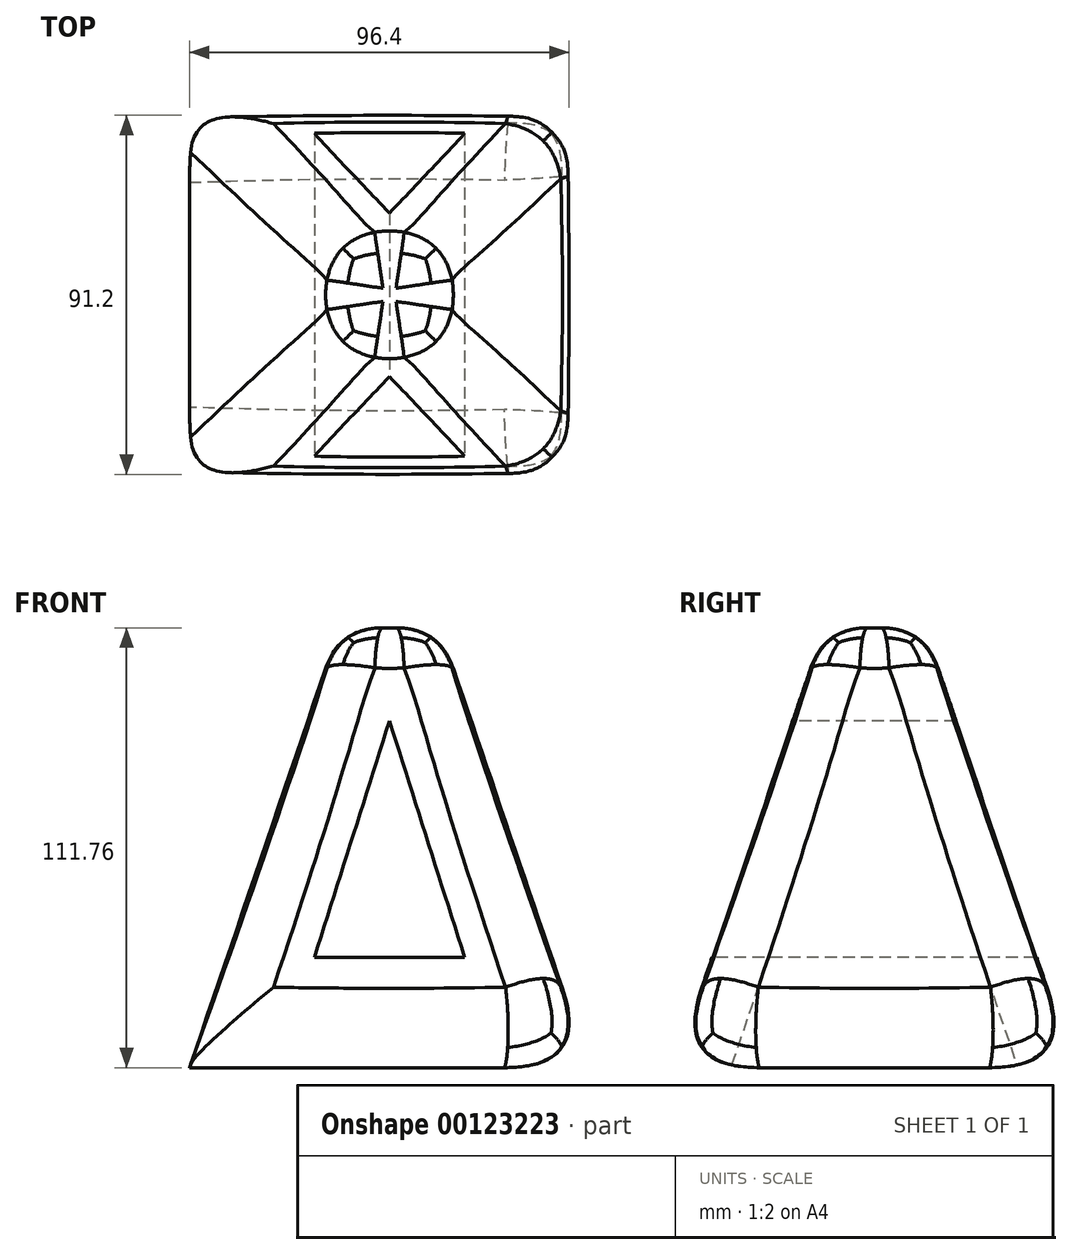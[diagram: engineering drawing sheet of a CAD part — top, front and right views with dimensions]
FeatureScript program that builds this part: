
annotation { "Feature Type Name" : "Feature", "Feature Type Description" : "" }
export const myFeature = defineFeature(function(context is Context, id is Id, definition is map)
    precondition{}
    {
        {
            var Q0;
            Q0=qCreatedBy(makeId("Top.planeOp"),FACE);
            cPlane(context, id + "F0", {"entities" : qUnion([Q0]), "cplaneType" : CPlaneType.OFFSET, "offset" : 111.76 * mm, "width" : 152.4 * mm, "height" : 152.4 * mm});
        }
        {
            var Q0;
            Q0=qCreatedBy(makeId("Top.planeOp"),FACE);
            var sketch = newSketch(context, id + "F1", { "sketchPlane" : qUnion([Q0])});
            skLineSegment(sketch, "E0.bottom", {"start": v(50.8, 50.8) * mm, "end": v(-50.8, 50.8) * mm});
            skLineSegment(sketch, "E0.top", {"start": v(50.8, -50.8) * mm, "end": v(-50.8, -50.8) * mm});
            skLineSegment(sketch, "E0.left", {"start": v(50.8, 50.8) * mm, "end": v(50.8, -50.8) * mm});
            skLineSegment(sketch, "E0.right", {"start": v(-50.8, 50.8) * mm, "end": v(-50.8, -50.8) * mm});
            skPoint(sketch, "E0.middle", {"position": v(0, 0) * mm});
            skSolve(sketch);
        }
        {
            var Q0;
            Q0=qCreatedBy(id+"F0.planeOp",FACE);
            var sketch = newSketch(context, id + "F2", { "sketchPlane" : qUnion([Q0])});
            skCircle(sketch, "E1", {"center": v(0, 0) * mm, "radius": 12.7 * mm});
            skSolve(sketch);
        }
        {
            var Q0;
            Q0=makeQuery(id+"F1.imprint","IMPRINT",FACE,{"disambiguationData":[TD([[makeQuery(id+"F1.imprint","IMPRINT",EDGE,{"derivedFrom":sQuery(id+"F1.wireOp",EDGE,"E0.bottom")}),1.0]])]});
            var Q1;
            Q1=makeQuery(id+"F2.imprint","IMPRINT",FACE,{"disambiguationData":[TD([[makeQuery(id+"F2.imprint","IMPRINT",EDGE,{"derivedFrom":sQuery(id+"F2.wireOp",EDGE,"E1")}),1.0]])]});
            loft(context, id + "F3", {"sheetProfilesArray" : [{ "sheetProfileEntities" : qUnion([Q0]) }, { "sheetProfileEntities" : qUnion([Q1]) }]});
        }
        {
            var Q0;
            {var subQ0=sQuery(id+"F2.wireOp",EDGE,"E1");var subQ1=sQuery(id+"F1.wireOp",EDGE,"E0.top");var subQ2=sQuery(id+"F1.wireOp",EDGE,"E0.right");var subQ3=sQuery(id+"F1.wireOp",EDGE,"E0.left");var subQ4=sQuery(id+"F1.wireOp",EDGE,"E0.bottom");Q0=makeQuery(id+"F3.opLoft","SWEPT_FACE",FACE,{"disambiguationData":[OSD([subQ4,subQ1,subQ3,subQ2,subQ0]),TDD([makeQuery(id+"F1.imprint","INTERSECT",VERTEX,{"derivedFrom":[subQ4,subQ2]}),makeQuery(id+"F1.imprint","INTERSECT",VERTEX,{"derivedFrom":[subQ1,subQ3]}),makeQuery(id+"F1.imprint","INTERSECT",VERTEX,{"derivedFrom":[subQ1,subQ2]}),makeQuery(id+"F1.imprint","IMPRINT",EDGE,{"derivedFrom":subQ1}),makeQuery(id+"F2.imprint","IMPRINT",EDGE,{"derivedFrom":subQ0})])]});}
            var Q1;
            {var subQ0=sQuery(id+"F2.wireOp",EDGE,"E1");var subQ1=sQuery(id+"F1.wireOp",EDGE,"E0.left");var subQ2=sQuery(id+"F1.wireOp",EDGE,"E0.right");var subQ3=sQuery(id+"F1.wireOp",EDGE,"E0.top");var subQ4=sQuery(id+"F1.wireOp",EDGE,"E0.bottom");Q1=makeQuery(id+"F3.opLoft","SWEPT_FACE",FACE,{"disambiguationData":[OSD([subQ4,subQ3,subQ1,subQ2,subQ0]),TDD([makeQuery(id+"F1.imprint","INTERSECT",VERTEX,{"derivedFrom":[subQ4,subQ1]}),makeQuery(id+"F1.imprint","INTERSECT",VERTEX,{"derivedFrom":[subQ3,subQ1]}),makeQuery(id+"F1.imprint","INTERSECT",VERTEX,{"derivedFrom":[subQ3,subQ2]}),makeQuery(id+"F1.imprint","IMPRINT",EDGE,{"derivedFrom":subQ1}),makeQuery(id+"F2.imprint","IMPRINT",EDGE,{"derivedFrom":subQ0})])]});}
            var Q2;
            {var subQ0=sQuery(id+"F2.wireOp",EDGE,"E1");var subQ1=sQuery(id+"F1.wireOp",EDGE,"E0.right");var subQ2=sQuery(id+"F1.wireOp",EDGE,"E0.top");var subQ3=sQuery(id+"F1.wireOp",EDGE,"E0.bottom");var subQ4=sQuery(id+"F1.wireOp",EDGE,"E0.left");Q2=makeQuery(id+"F3.opLoft","SWEPT_FACE",FACE,{"disambiguationData":[OSD([subQ3,subQ2,subQ4,subQ1,subQ0]),TDD([makeQuery(id+"F1.imprint","INTERSECT",VERTEX,{"derivedFrom":[subQ3,subQ4]}),makeQuery(id+"F1.imprint","INTERSECT",VERTEX,{"derivedFrom":[subQ3,subQ1]}),makeQuery(id+"F1.imprint","INTERSECT",VERTEX,{"derivedFrom":[subQ2,subQ1]}),makeQuery(id+"F1.imprint","IMPRINT",EDGE,{"derivedFrom":subQ1}),makeQuery(id+"F2.imprint","IMPRINT",EDGE,{"derivedFrom":subQ0})])]});}
            var Q3;
            Q3=makeQuery(id+"F3.opLoft","SWEPT_FACE",FACE,{"disambiguationData":[OSD([sQuery(id+"F1.wireOp",EDGE,"E0.bottom"),sQuery(id+"F1.wireOp",EDGE,"E0.left"),sQuery(id+"F1.wireOp",EDGE,"E0.right"),sQuery(id+"F2.wireOp",EDGE,"E1")])]});
            fillet(context, id + "F4", {"entities" : qUnion([Q0, Q1, Q2, Q3]), "radius" : 15.24 * mm, "tangentPropagation" : true, "rho" : 0.5, "crossSection" : FilletCrossSection.CONIC, "allowEdgeOverflow" : false});
        }
        {
            var Q0;
            Q0=qCreatedBy(makeId("Front.planeOp"),FACE);
            var sketch = newSketch(context, id + "F5", { "sketchPlane" : qUnion([Q0])});
            skPoint(sketch, "E2.0", {"position": v(-29.5, 20.43) * mm});
            skPoint(sketch, "E3.0", {"position": v(29.5, 20.43) * mm});
            skPoint(sketch, "E4.0", {"position": v(3.7, 101.6) * mm});
            skPoint(sketch, "E5.0", {"position": v(-3.7, 101.6) * mm});
            skLineSegment(sketch, "E6.0", {"start": v(19.08, 28.05) * mm, "end": v(0, 88.1) * mm});
            skLineSegment(sketch, "E6.1", {"start": v(-19.08, 28.05) * mm, "end": v(19.08, 28.05) * mm});
            skLineSegment(sketch, "E6.2", {"start": v(0, 88.1) * mm, "end": v(-19.08, 28.05) * mm});
            skSolve(sketch);
        }
        {
            var Q0;
            Q0 = qSketchRegion(id + "F5", true);
            extrude(context, id + "F6", {"entities" : qUnion([Q0]), "operationType" : NewBodyOperationType.REMOVE, "endBound" : BoundingType.THROUGH_ALL, "oppositeDirection" : true, "depth" : 25.4 * mm, "hasSecondDirection" : true, "secondDirectionBound" : SecondDirectionBoundingType.THROUGH_ALL, "secondDirectionOppositeDirection" : false, "secondDirectionDepth" : 25.4 * mm});
        }
    });
